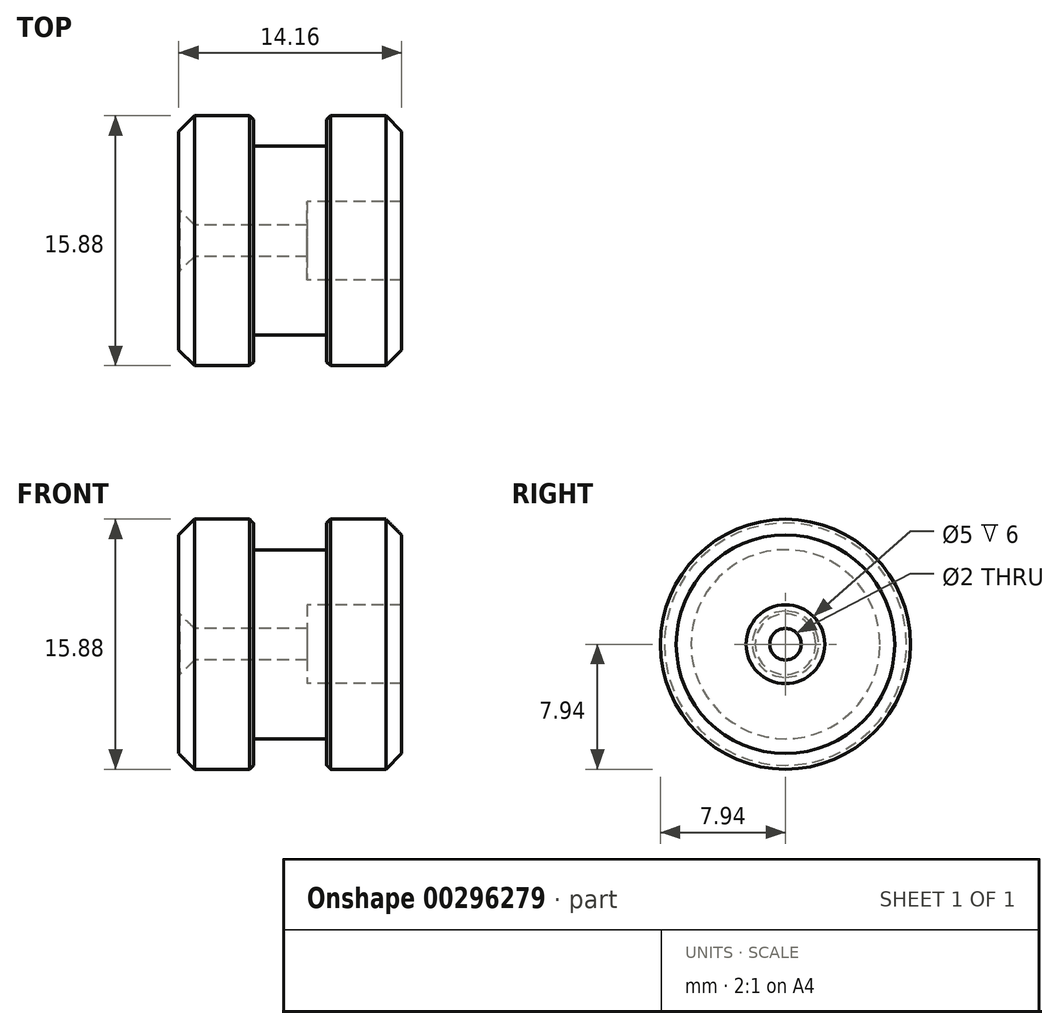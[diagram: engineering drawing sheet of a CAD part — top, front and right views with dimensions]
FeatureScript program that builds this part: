
annotation { "Feature Type Name" : "Feature", "Feature Type Description" : "" }
export const myFeature = defineFeature(function(context is Context, id is Id, definition is map)
    precondition{}
    {
        {
            var Q0;
            Q0=qCreatedBy(makeId("Top.planeOp"),FACE);
            var sketch = newSketch(context, id + "F0", { "sketchPlane" : qUnion([Q0])});
            skLineSegment(sketch, "E0", {"start": v(0, 0) * mm, "end": v(14.16, 0) * mm});
            skLineSegment(sketch, "E1", {"start": v(14.16, 0) * mm, "end": v(14.16, 7.94) * mm});
            skLineSegment(sketch, "E2", {"start": v(14.16, 7.94) * mm, "end": v(9.4, 7.94) * mm});
            skLineSegment(sketch, "E3", {"start": v(9.4, 7.94) * mm, "end": v(9.4, 6) * mm});
            skLineSegment(sketch, "E4", {"start": v(9.4, 6) * mm, "end": v(4.76, 6) * mm});
            skLineSegment(sketch, "E5", {"start": v(4.76, 6) * mm, "end": v(4.76, 7.94) * mm});
            skLineSegment(sketch, "E6", {"start": v(4.76, 7.94) * mm, "end": v(0, 7.94) * mm});
            skLineSegment(sketch, "E7", {"start": v(0, 7.94) * mm, "end": v(0, 0) * mm});
            skLineSegment(sketch, "E8", {"start": v(0, 1) * mm, "end": v(0, 1) * mm});
            skLineSegment(sketch, "E9", {"start": v(8.16, 1) * mm, "end": v(8.16, 2.5) * mm});
            skLineSegment(sketch, "E10", {"start": v(8.16, 2.5) * mm, "end": v(14.16, 2.5) * mm});
            skLineSegment(sketch, "E11", {"start": v(0, 1) * mm, "end": v(8.16, 1) * mm});
            skLineSegment(sketch, "E12", {"start": v(14.16, 2.5) * mm, "end": v(14.16, 2.5) * mm});
            skSolve(sketch);
        }
        {
            var Q0;
            {var subQ0=sQuery(id+"F0.wireOp",EDGE,"E2");Q0=makeQuery(id+"F0.imprint","IMPRINT",FACE,{"disambiguationData":[TD([[makeQuery(id+"F0.imprint","IMPRINT",EDGE,{"derivedFrom":subQ0}),1.0]])]});}
            var Q1;
            Q1=sQuery(id+"F0.wireOp",EDGE,"E0");
            revolve(context, id + "F1", {"entities" : qUnion([Q0]), "axis" : qUnion([Q1]), "revolveType" : RevolveType.FULL});
        }
        {
            var Q0;
            Q0=makeQuery(id+"F1.opRevolve","SWEPT_EDGE",EDGE,{"disambiguationData":[OSD([sQuery(id+"F0.wireOp",EDGE,"E6"),sQuery(id+"F0.wireOp",EDGE,"E7")])]});
            var Q1;
            Q1=makeQuery(id+"F1.opRevolve","SWEPT_EDGE",EDGE,{"disambiguationData":[OSD([sQuery(id+"F0.wireOp",EDGE,"E1"),sQuery(id+"F0.wireOp",EDGE,"E2")])]});
            var Q2;
            Q2=makeQuery(id+"F1.opRevolve","SWEPT_EDGE",EDGE,{"disambiguationData":[OSD([sQuery(id+"F0.wireOp",EDGE,"E7"),sQuery(id+"F0.wireOp",EDGE,"E11")])]});
            chamfer(context, id + "F2", {"entities" : qUnion([Q0, Q1, Q2]), "width" : 1 * mm, "tangentPropagation" : true});
        }
        {
            var Q0;
            Q0=makeQuery(id+"F1.opRevolve","SWEPT_EDGE",EDGE,{"disambiguationData":[OSD([sQuery(id+"F0.wireOp",EDGE,"E5"),sQuery(id+"F0.wireOp",EDGE,"E6")])]});
            var Q1;
            Q1=makeQuery(id+"F1.opRevolve","SWEPT_EDGE",EDGE,{"disambiguationData":[OSD([sQuery(id+"F0.wireOp",EDGE,"E2"),sQuery(id+"F0.wireOp",EDGE,"E3")])]});
            var Q2;
            {var subQ0=sQuery(id+"F0.wireOp",EDGE,"E7");Q2=makeQuery(id+"F2.opChamfer","BLEND_EDGE",EDGE,{"blendedFrom":[makeQuery(id+"F1.opRevolve","SWEPT_EDGE",EDGE,{"disambiguationData":[OSD([subQ0,sQuery(id+"F0.wireOp",EDGE,"E11")])]}),makeQuery(id+"F1.opRevolve","SWEPT_FACE",FACE,{"disambiguationData":[OSD([subQ0])]})],"blendedInto":[makeQuery(id+"F1.opRevolve","SWEPT_FACE",FACE,{"disambiguationData":[OSD([subQ0])]})]});}
            chamfer(context, id + "F3", {"entities" : qUnion([Q0, Q1, Q2]), "width" : 0.25 * mm, "tangentPropagation" : true});
        }
    });
